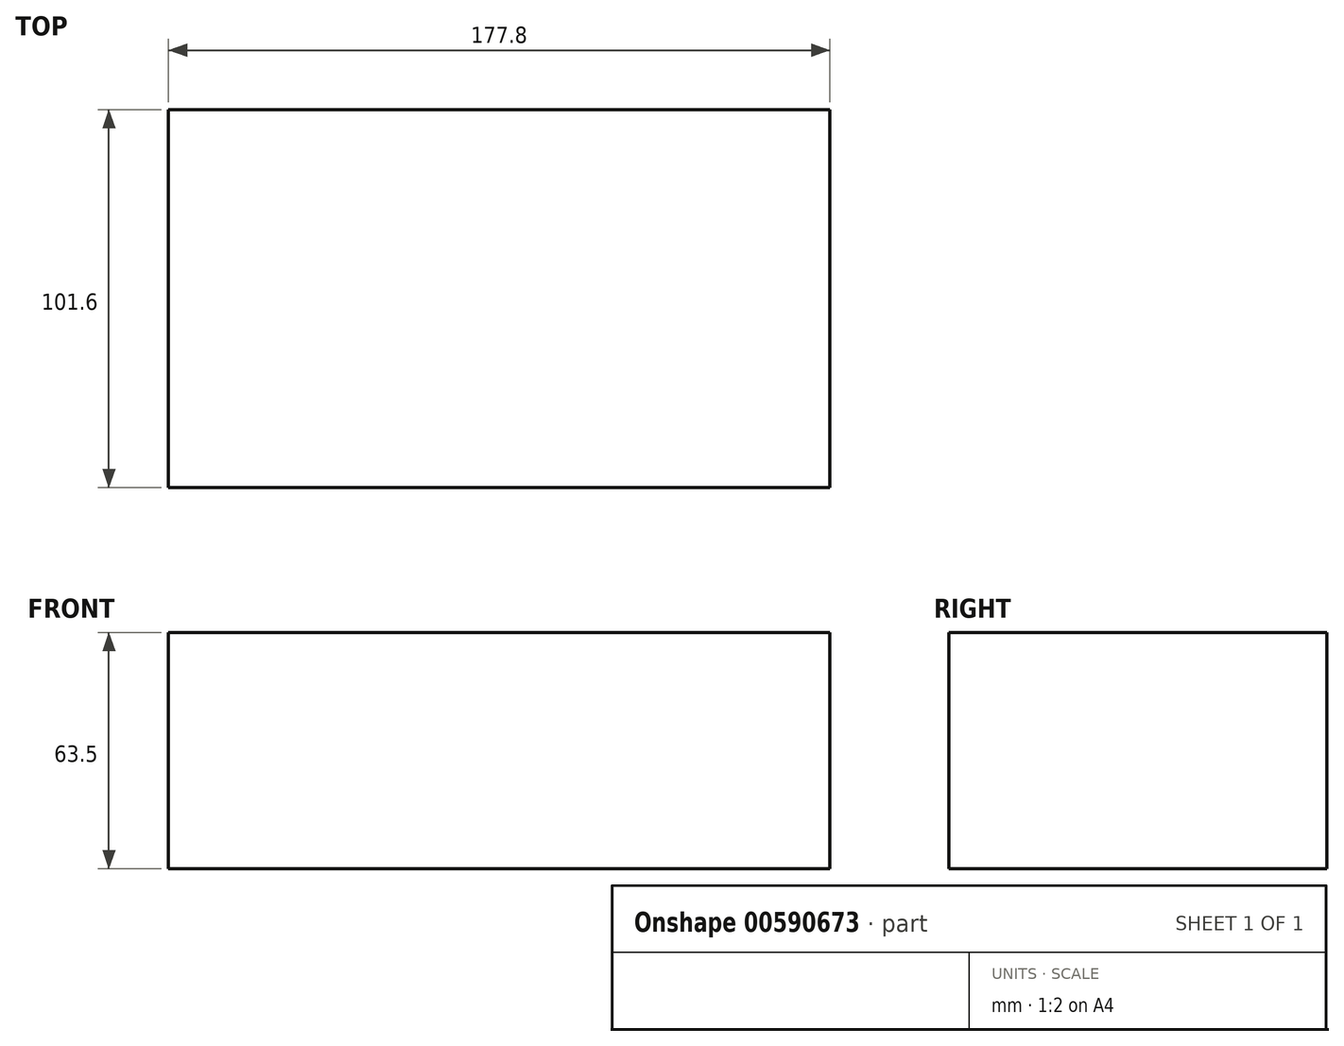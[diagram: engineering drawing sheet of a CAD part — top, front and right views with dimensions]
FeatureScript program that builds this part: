
annotation { "Feature Type Name" : "Feature", "Feature Type Description" : "" }
export const myFeature = defineFeature(function(context is Context, id is Id, definition is map)
    precondition{}
    {
        {
            var Q0;
            Q0=qCreatedBy(makeId("Top.planeOp"),FACE);
            var sketch = newSketch(context, id + "F0", { "sketchPlane" : qUnion([Q0])});
            skLineSegment(sketch, "E0.bottom", {"start": v(88.9, -50.8) * mm, "end": v(-88.9, -50.8) * mm});
            skLineSegment(sketch, "E0.top", {"start": v(88.9, 50.8) * mm, "end": v(-88.9, 50.8) * mm});
            skLineSegment(sketch, "E0.left", {"start": v(88.9, -50.8) * mm, "end": v(88.9, 50.8) * mm});
            skLineSegment(sketch, "E0.right", {"start": v(-88.9, -50.8) * mm, "end": v(-88.9, 50.8) * mm});
            skPoint(sketch, "E0.middle", {"position": v(0, 0) * mm});
            skSolve(sketch);
        }
        {
            var Q0;
            Q0=makeQuery(id+"F0.imprint","IMPRINT",FACE,{"disambiguationData":[TD([[makeQuery(id+"F0.imprint","IMPRINT",EDGE,{"derivedFrom":sQuery(id+"F0.wireOp",EDGE,"E0.bottom")}),-1.0]])]});
            extrude(context, id + "F1", {"entities" : qUnion([Q0]), "depth" : 63.5 * mm, "offsetDistance" : 25.4 * mm});
        }
    });
